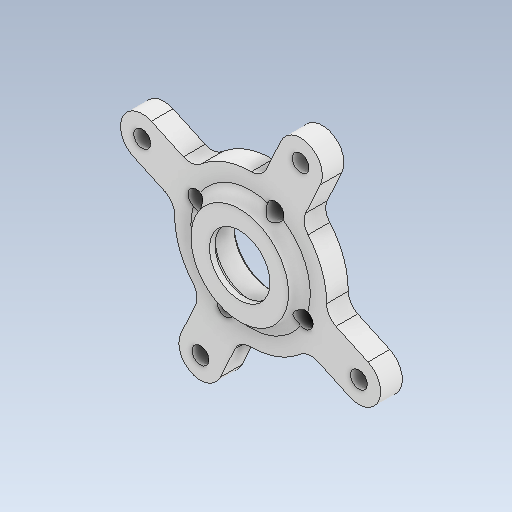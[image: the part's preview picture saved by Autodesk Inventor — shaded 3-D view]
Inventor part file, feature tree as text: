
AUTODESK INVENTOR PART (.ipt)
format: ipt  version: 2020 (Build 240168000, 168)  size: 412,672 bytes
history: native  units: mm
features: sketch x5, extrude x4, projected_geometry x3, other x3, pattern_circular x2, fillet x2, chamfer x2, reference x2, hole x1
ambient origin geometry x8: Origin, YZ Plane, XZ Plane, XY Plane, X Axis, Y Axis, Z Axis, Center Point
bodies: Solid1 (feature_tree)
feature tree (24):
  extrude  "Extrusion1"  Depth=28.0mm
  extrude  "Extrusion2"  Depth=8.0mm
  pattern_circular  "Circular Pattern1"  Count=4 Angle=360.0deg
  hole  "Hole1"  [1 undecoded]
  fillet  "Fillet1"  Radius=11.0mm
  extrude  "Extrusion3"  Depth=2.0mm
  pattern_circular  "Circular Pattern2"  [2 undecoded]
  extrude  "Extrusion4"  Depth=2.0mm TaperAngle=360.0deg
  chamfer  "Chamfer2"  Distance=18.0mm
  chamfer  "Chamfer3"  Distance=1.0mm
  fillet  "Fillet2"  Radius=2.0mm
  sketch  "Sketch1"  dims[d0=13.15mm d1=28.0mm]
  reference  "Reference1"
  sketch  "Sketch2"  dims[d2=4.0mm d3=0.0mm d4=8.0mm]
  reference  "Reference2"
  projected_geometry  "Projected Loop1"
  sketch  "Sketch3"  dims[d5=8.0mm]
  projected_geometry  "Projected Loop2"
  sketch  "Sketch4"  dims[d6=4.0mm d7=0.0mm d8=40.0mm d9=360.0deg]
  projected_geometry  "Projected Loop3"
  sketch  "Sketch5"  dims[d11=3.1mm d12=6.0mm d13=4.0mm d14=2.0mm d15=90.0deg d16=17.0mm d17=0.0mm d18=3.0mm d19=11.0mm d20=3.1mm d21=4.0mm d22=0.0mm d23=40.0mm d24=360.0deg d29=18.0mm d30=1.0mm d31=2.0mm d32=0.0mm d33=1.0mm d34=2.0mm d35=45.0deg d36=0.5mm d37=2.0mm d38=45.0deg d39=2.0mm]
  parser-record x1  (decoder bookkeeping rows leaked as tree rows — omitted from the tree; the rows remain in map.json)
  other  "reducer_2.iam"
  other  "motor_h_1:1"
note: 3 required parameter values undecoded (feature->parameter linkage not recoverable at this tier; creation-order binding heuristic only, values carry confidence <= 0.55)
note: 1 file-system path scrubbed to <path> (originals preserved in map.json)
